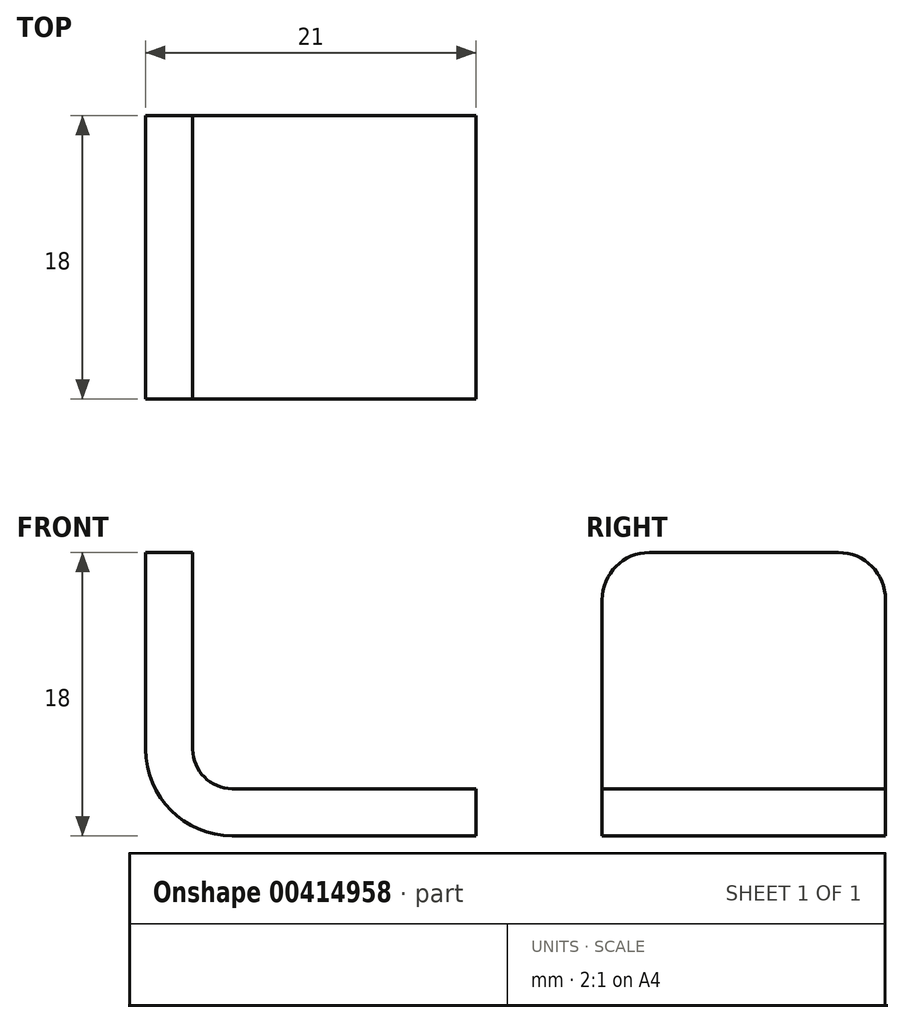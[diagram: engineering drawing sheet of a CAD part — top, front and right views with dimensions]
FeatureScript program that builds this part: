
annotation { "Feature Type Name" : "Feature", "Feature Type Description" : "" }
export const myFeature = defineFeature(function(context is Context, id is Id, definition is map)
    precondition{}
    {
        {
            var Q0;
            Q0=qCreatedBy(makeId("Front.planeOp"),FACE);
            var sketch = newSketch(context, id + "F0", { "sketchPlane" : qUnion([Q0])});
            skLineSegment(sketch, "E0", {"start": v(5.5, 0) * mm, "end": v(21, 0) * mm});
            skLineSegment(sketch, "E1", {"start": v(21, 0) * mm, "end": v(21, 3) * mm});
            skLineSegment(sketch, "E2", {"start": v(21, 3) * mm, "end": v(5.5, 3) * mm});
            skLineSegment(sketch, "E3", {"start": v(3, 5.5) * mm, "end": v(3, 18) * mm});
            skLineSegment(sketch, "E4", {"start": v(3, 18) * mm, "end": v(0, 18) * mm});
            skLineSegment(sketch, "E5", {"start": v(0, 18) * mm, "end": v(0, 5.5) * mm});
            skPoint(sketch, "E6.visualSharp", {"position": v(3, 3) * mm});
            skArc(sketch, "E6.filletArc", {"start": v(3, 5.5) * mm, "mid": v(3.73, 3.73) * mm, "end": v(5.5, 3) * mm});
            skPoint(sketch, "E7.visualSharp", {"position": v(0, 0) * mm});
            skArc(sketch, "E7.filletArc", {"start": v(0, 5.5) * mm, "mid": v(1.61, 1.61) * mm, "end": v(5.5, 0) * mm});
            skSolve(sketch);
        }
        {
            var Q0;
            Q0=makeQuery(id+"F0.imprint","IMPRINT",FACE,{"disambiguationData":[TD([[makeQuery(id+"F0.imprint","IMPRINT",EDGE,{"derivedFrom":sQuery(id+"F0.wireOp",EDGE,"E0")}),1.0]])]});
            extrude(context, id + "F1", {"entities" : qUnion([Q0]), "depth" : 18 * mm});
        }
        {
            var Q0;
            Q0=makeQuery(id+"F1.opExtrude","CAP_EDGE",EDGE,{"disambiguationData":[OSD([sQuery(id+"F0.wireOp",EDGE,"E4")])],"isStart":false});
            var Q1;
            Q1=makeQuery(id+"F1.opExtrude","CAP_EDGE",EDGE,{"disambiguationData":[OSD([sQuery(id+"F0.wireOp",EDGE,"E4")])],"isStart":true});
            fillet(context, id + "F2", {"entities" : qUnion([Q0, Q1]), "radius" : 3 * mm, "tangentPropagation" : true, "allowEdgeOverflow" : false});
        }
    });
